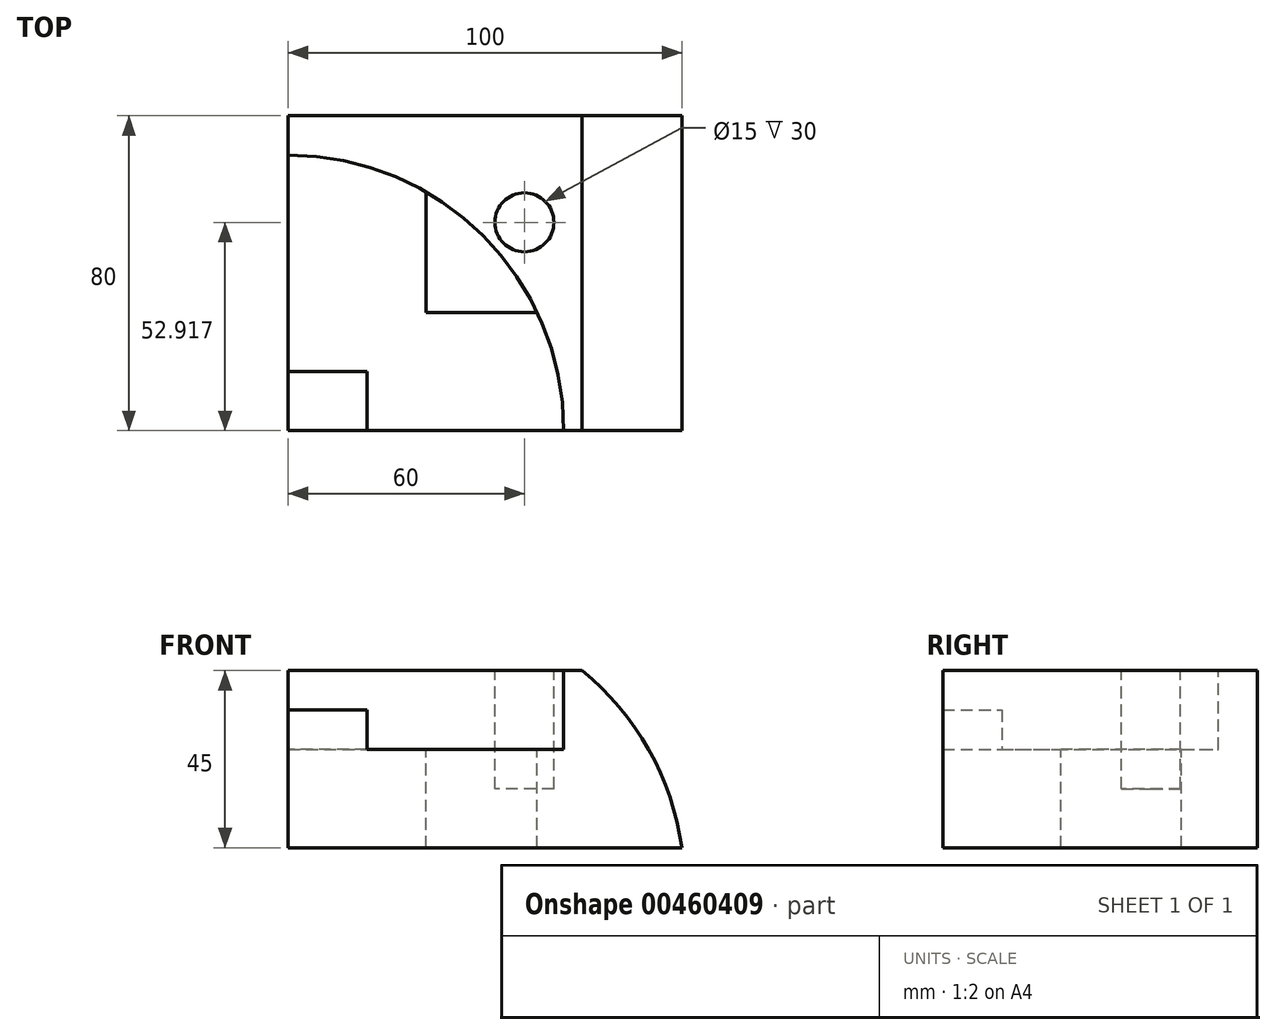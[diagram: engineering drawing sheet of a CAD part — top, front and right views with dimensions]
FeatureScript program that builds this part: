
annotation { "Feature Type Name" : "Feature", "Feature Type Description" : "" }
export const myFeature = defineFeature(function(context is Context, id is Id, definition is map)
    precondition{}
    {
        {
            var Q0;
            Q0=qCreatedBy(makeId("Top.planeOp"),FACE);
            var sketch = newSketch(context, id + "F0", { "sketchPlane" : qUnion([Q0])});
            skLineSegment(sketch, "E0.bottom", {"start": v(0, 0) * mm, "end": v(100, 0) * mm});
            skLineSegment(sketch, "E0.top", {"start": v(0, 80) * mm, "end": v(100, 80) * mm});
            skLineSegment(sketch, "E0.left", {"start": v(0, 0) * mm, "end": v(0, 80) * mm});
            skLineSegment(sketch, "E0.right", {"start": v(100, 0) * mm, "end": v(100, 80) * mm});
            skSolve(sketch);
        }
        {
            var Q0;
            Q0 = qSketchRegion(id + "F0", true);
            extrude(context, id + "F1", {"entities" : qUnion([Q0]), "depth" : 45 * mm});
        }
        {
            var Q0;
            Q0=makeQuery(id+"F1.opExtrude","CAP_FACE",FACE,{"disambiguationData":[OSD([sQuery(id+"F0.wireOp",EDGE,"E0.bottom"),sQuery(id+"F0.wireOp",EDGE,"E0.top"),sQuery(id+"F0.wireOp",EDGE,"E0.left"),sQuery(id+"F0.wireOp",EDGE,"E0.right")])],"isStart":false});
            var sketch = newSketch(context, id + "F2", { "sketchPlane" : qUnion([Q0])});
            skCircle(sketch, "E1", {"center": v(60, 52.92) * mm, "radius": 7.5 * mm});
            skSolve(sketch);
        }
        {
            var Q0;
            Q0 = qSketchRegion(id + "F2", true);
            extrude(context, id + "F3", {"entities" : qUnion([Q0]), "operationType" : NewBodyOperationType.REMOVE, "oppositeDirection" : true, "depth" : 30 * mm});
        }
        {
            var Q0;
            Q0=makeQuery(id+"F1.opExtrude","CAP_FACE",FACE,{"disambiguationData":[OSD([sQuery(id+"F0.wireOp",EDGE,"E0.bottom"),sQuery(id+"F0.wireOp",EDGE,"E0.top"),sQuery(id+"F0.wireOp",EDGE,"E0.left"),sQuery(id+"F0.wireOp",EDGE,"E0.right")])],"isStart":false});
            var sketch = newSketch(context, id + "F4", { "sketchPlane" : qUnion([Q0])});
            skCircle(sketch, "E2", {"center": v(0, 0) * mm, "radius": 70 * mm});
            skSolve(sketch);
        }
        {
            var Q0;
            Q0 = qSketchRegion(id + "F4", true);
            extrude(context, id + "F5", {"entities" : qUnion([Q0]), "operationType" : NewBodyOperationType.REMOVE, "oppositeDirection" : true, "depth" : 20 * mm});
        }
        {
            var Q0;
            Q0=makeQuery(id+"F5.boolean.opBoolean","COPY",FACE,{"derivedFrom":makeQuery(id+"F5.opExtrude","CAP_FACE",FACE,{"disambiguationData":[OSD([sQuery(id+"F4.wireOp",EDGE,"E2")])],"isStart":false})});
            var sketch = newSketch(context, id + "F6", { "sketchPlane" : qUnion([Q0])});
            skLineSegment(sketch, "E3.bottom", {"start": v(0, 0) * mm, "end": v(20, 0) * mm});
            skLineSegment(sketch, "E3.top", {"start": v(0, 15) * mm, "end": v(20, 15) * mm});
            skLineSegment(sketch, "E3.left", {"start": v(0, 0) * mm, "end": v(0, 15) * mm});
            skLineSegment(sketch, "E3.right", {"start": v(20, 0) * mm, "end": v(20, 15) * mm});
            skSolve(sketch);
        }
        {
            var Q0;
            Q0 = qSketchRegion(id + "F6", true);
            extrude(context, id + "F7", {"entities" : qUnion([Q0]), "operationType" : NewBodyOperationType.ADD, "depth" : 10 * mm});
        }
        {
            var Q0;
            Q0=makeQuery(id+"F5.boolean.opBoolean","COPY",FACE,{"derivedFrom":makeQuery(id+"F5.opExtrude","CAP_FACE",FACE,{"disambiguationData":[OSD([sQuery(id+"F4.wireOp",EDGE,"E2")])],"isStart":false})});
            var sketch = newSketch(context, id + "F8", { "sketchPlane" : qUnion([Q0])});
            skLineSegment(sketch, "E4", {"start": v(35, 60.62) * mm, "end": v(35, 30) * mm});
            skLineSegment(sketch, "E5", {"start": v(35, 30) * mm, "end": v(63.25, 30) * mm});
            skCircle(sketch, "E6", {"center": v(0, 0) * mm, "radius": 70 * mm});
            skSolve(sketch);
        }
        {
            var Q0;
            {var subQ0=sQuery(id+"F8.wireOp",EDGE,"E4");Q0=makeQuery(id+"F8.imprint","IMPRINT",FACE,{"disambiguationData":[TD([[makeQuery(id+"F8.imprint","IMPRINT",EDGE,{"derivedFrom":subQ0}),1.0]])]});}
            extrude(context, id + "F9", {"entities" : qUnion([Q0]), "operationType" : NewBodyOperationType.REMOVE, "endBound" : BoundingType.THROUGH_ALL, "oppositeDirection" : true, "depth" : 25 * mm});
        }
        {
            var Q0;
            Q0=makeQuery(id+"F7.boolean.opBoolean","MERGE",FACE,{"derivedFrom":[makeQuery(id+"F1.opExtrude","SWEPT_FACE",FACE,{"disambiguationData":[OSD([sQuery(id+"F0.wireOp",EDGE,"E0.bottom")])]}),makeQuery(id+"F7.opExtrude","SWEPT_FACE",FACE,{"disambiguationData":[OSD([sQuery(id+"F6.wireOp",EDGE,"E3.bottom")])]})]});
            var sketch = newSketch(context, id + "F10", { "sketchPlane" : qUnion([Q0])});
            skCircle(sketch, "E7", {"center": v(30.65, -9.5) * mm, "radius": 70 * mm});
            skPoint(sketch, "E7.first.point", {"position": v(100, 0) * mm});
            skPoint(sketch, "E7.second.point", {"position": v(-38.7, 0) * mm});
            skPoint(sketch, "E7.third.point", {"position": v(74.58, 45) * mm});
            skSolve(sketch);
        }
        {
            var Q0;
            {var subQ1=sQuery(id+"F0.wireOp",EDGE,"E0.bottom");var subQ2=makeQuery(id+"F1.opExtrude","SWEPT_EDGE",EDGE,{"disambiguationData":[OSD([subQ1,sQuery(id+"F0.wireOp",EDGE,"E0.right")])]});Q0=makeQuery(id+"F10.imprint","IMPRINT",FACE,{"disambiguationData":[TD([[makeQuery(id+"F10.imprint","IMPRINT",EDGE,{"derivedFrom":subQ2}),-1.0]])]});}
            extrude(context, id + "F11", {"entities" : qUnion([Q0]), "operationType" : NewBodyOperationType.REMOVE, "endBound" : BoundingType.THROUGH_ALL, "oppositeDirection" : true, "depth" : 25 * mm});
        }
    });
